# Revit family: Central de Alarme de Incêndio Analógica CYGNUS-SE ILUMAC
name_source: partatom
category: Dispositivos de alarme de incêndio
units: mm (PartAtom-declared; Revit-internal decimal feet)

## family parameters
Com base no plano de trabalho = Não
Compartilhado = Não
Corte com vazios quando carregada = Não
Cota do conector redondo = Utilizar diâmetro
Manter orientação da anotação = Não
Número OmniClass = 23.75.00.00
Ponto de cálculo do ambiente = Não
Sempre na vertical = Sim
Tipo de parte = Normal
Título OmniClass = Climate Control (HVAC)

## types (2) — shared parameters
Alimentação principal da rede elétrica = 100 à 240VCA – 60Hz
Alimentação secundária = 24Vcc (2 baterias seladas de 12Vcc 2,2Ah)
Baterias recomendadas = 12V @ 2,2 A/h. VRLA
Bornes para conexão dos condutores = Máximo 2,5mm²
Capacitância máxima do cabo = 120pF/m
Característica máxima do cabo dos laços = Capacitância = 120pF/m | Resistência = 25Ω/Km
Comprimento máx. do laço (recomendado) = 1.500 metros linear
Comprimento máximo do cabo (linear) = 1.000m com 1,5mm² / 1.500m com 2,5mm²
Conexão com Software Programador PUC-D = Necessário o uso do módulo de interface, adquirido
separadamente
Consumo de energia da rede elétrica = 115 Watts
Corrente de ativação do laço em alarme = 10mA @ 06Vcc (+/- 1V)
Corrente de recarga das baterias = 500mA @ 27,6Vcc nominal (25ºC)
Corrente máx. por laço em supervisão = 300mA @ 27Vcc
Corrente máxima no laço em alarme = 38mA
Dimensões (AxLxP) = 255x230x100mm
Distrib. das cargas da fonte em alarme para circuitos internos = 180mA
Distrib. das cargas da fonte em alarme para saída auxiliar de alimentação V+ = 400mA
Distrib. das cargas da fonte em repouso para circuitos internos = 180mA
Distrib. das cargas da fonte em repouso para o recarregador de baterias = 500mA
Distribuição das cargas da fonte em alarme = 20mA para circuitos internos.
460mA para os laços de detecção.
2A total para o circuito de sirenes pela bateria
Distribuição das cargas da fonte em repouso = 20mA para circuitos internos.
460mA para os laços de detecção.
400mA para o recarregador de baterias.
Fabricante = ILUMAC
Fixação = Caixa de sobrepor com 4 entradas para tubo 3/4”
Grau de proteção = IP30 (uso interno)
Grupos e Zonas = 1
Impedância do drive de comunicação = 320KΩ (por laço)
Log de eventos = 5.000 últimas ocorrências
Material da caixa = Plástico ABS branco
Normas técnicas aplicáveis = NBR 17240
Painel frontal (IHM) = 9 LEDs / 10 teclas / LCD 2x16 c/ backlight de LED
Painéis Repetidores = Suporta até 2 painéis repetidores
Peso = 1,5 Kg (sem baterias)
4,3 Kg (com 2 baterias de 12Vcc 2,2Ah)

4,3 Kg (com 2 baterias de 12Vcc 2,2Ah)
1,8 kg (com 1 bateria de 12V 2,2 A/h)
2,6 kg (com 2 bateria de 12V 2,2 A/h)
Proteção de curto-circuito por laço = Fusível eletrônico 500mA @ 24Vcc (25ºC)
Proteção de curto-circuito saída de sirenes = Fusível rearmável - PTC 1,5A @ 24Vcc (25ºC)
Proteção na entrada da rede elétrica = Fusível 20AG-2A (fusão rápida)

Termistor NTC 10R
Proteção na entrada das baterias = Fusível de vidro 20AG- 3A (fusão rápida)
Proteção na recarga das baterias = Fusível rearmável - PTC 1,5A @ 24Vcc (25ºC)
Protocolo de comunicação = Cygnus (proprietário)
Quant. de sirenes com alim. externa = No máximo 32 sirenes
(entre alimentação interna e externa)
Quant. máxima de sirenes alimentadas pelo laço = 20
Quant. máxima de sirenes endereçáveis por laço = 32*
Quantidade de dispositivos de saída endereçáveis por laço (sirenes-módulos) = Até 30 dispositivos de saída (consulte o manual)
Quantidade de dispositivos por laços-zonas 2 = 20
Quantidade de laços-zonas = 6 setores
Recarregador das baterias = 400mA @ 27,6Vcc nominal 25oC
Resistência máxima do cabo = 25 ohms/Km
Saída da fonte de alimentação = 2,5A @ 28Vcc (25ºC)
Saída para sirenes convencionais = 1 saída de 900mA @ 24Vcc supervisionada
Saída rele auxiliar = 1x saída contato seco 1A @ 30V p/ aviso de alarme
1x saída contato seco 1A @ 30V p/ aviso de falha
(ambas – carga resistiva)
(carga resistiva)
Secção dos condutores do cabo = Mínima de 1,5mm² e máxima de 2,5mm²
Sinalizações = Visual e sonora para alarme e falha
Temperatura de operação = 0 à 40ºC
Tensão de ativação dos laços = < 06V
Tensão nominal e de operação = 24Vcc (21 à 28Vcc)
Topologia = Classe A – Linear (2 fios)
Umidade relativa = Máximo 95% sem condensação
Área de cobertura máxima por laço = 1.600m²
zero-valued in all types: Elevação padrão

## per-type parameters (varying)
| type | Código do produto | Descrição | Distrib. das cargas da fonte em alarme para o recarregador de baterias | Distrib. das cargas da fonte em alarme para os laços endereçáveis de detecção | Distrib. das cargas da fonte em alarme para saída Sirene | Distrib. das cargas da fonte em repouso para os laços endereçáveis de detecção | Distrib. das cargas da fonte em repouso para saída auxiliar de alimentação V+ | Quantidade máxima de endereços |
| CYGNUS-SE 125 1LA | 007002 | Central de Alarme de Incêndio Analógica CYGNUS-SE 125 1LA | 400mA | 300mA | 900mA | 300mA | 400mA | 125 |
| CYGNUS-SE 250 2LA | 007003 | Central de Alarme de Incêndio Analógica CYGNUS-SE 250 2LA | 200mA por laço | 300mA por laço | 500mA | 300mA por laço | 200mA por laço | 250 |

note: column(s) folded — value = type name in every type: Modelo
